# Revit family: HVAC_Fireplaces_Regency-Fireplace_Grandview-gas-fireplace_G600EC
name_source: partatom
category: Specialty Equipment
units: mm (PartAtom-declared; Revit-internal decimal feet)

## family parameters
Classification Number = 23.40.20.34.14
Cut with Voids When Loaded = No
Enable Cutting in Views = No
Host = Face
Maintain Annotation Orientation = No
Part Type = Normal
Room Calculation Point = No
Round Connector Dimension = Use Diameter
Shared = No

## types (2) — shared parameters
Apparent Load = 0 VA
Clean Front - Cool wall Installation = Clean Front - Cool wall Installation
Clean Front - Non-Combustible Installation = Clean Front - Non-Combustible Installation
Current = 2 A
Depth = 15 "
Description = Choose stunning flame picture, choose your accessories, and create a one-of-a-kind fireplace. The Regency Grandview series of gas fireplaces are designed to maximize choice and customization letting you pick and choose everything so you get the fireplace of your dreams.
Duct Connector Description = 4” Inner / 6-5/8” Outer
Duct Diameter = 7 "
Frequency = 60 Hz
Gas flow = 0.0 L/s
Height = 30 "
Housing Material = Regency Fireplace - Metal - Black
Manufacturer = Regency Fireplace
Number of Poles = 1
Outside Finish w-Faceplate - Non-Combustible Installation = Outside Finish w-Faceplate - Non-Combustible Installation
Outside Finish w-Finishing Trim - Cool wall Installation = Outside Finish w-Finishing Trim - Cool wall Installation
Pipe Diameter = 1 "
Power Consumption = 0 W
Power Factor = 1
Product Documentation Link = https://assets.regency-fire.com
Product Page URL = https://www.regency-fire.com
Product data url = https://www.bimobject.com
URL = https://www.regency-fire.com
Ventilation flow = 100.0 CFM
Voltage = 120 V
Width = 32 "
zero-valued in all types: Default Elevation, Version

## per-type parameters (varying)
| type | CSA P.4.1 | Fuel Type | Gas Connector Description | Manifold Pressure - High | Manifold Pressure - Low | Maximum Input Altitude 0-4500 ft. (0-1372m) | Minimum Input Altitude 0-4500 ft. (0-1372m) | Minimum Supply Pressure | Orifce Size -Altitude 0-4500 ft |
| G600EC-NG | 64.8% | Natural Gas | Natural gas supply | 3.8” W.C. (0.94 kPa) | 1.1” W.C. (0.27 kPa) | 21,000 Btu/h (3.37 kW) | 11,500 Btu/h (3.37 kW) | 5” W.C. (1.25 kPa) | # 46 DMS |
| G600EC-LP | 67.22% | Propane | Propane gas supply | 10” W.C. (2.49 kPa) | 6.4” W.C. (1.60 kPa) | 20,500 Btu/h (6.01 kW) | 16,500 Btu/h (4.84 kW) | 11” W.C. (2.74 kPa) | # 55 DMS |

note: column(s) folded — value = type name in every type: Model

## geometry (parser evidence)
native form markers: Sweep x16
no freeform markers — native parametric forms only
